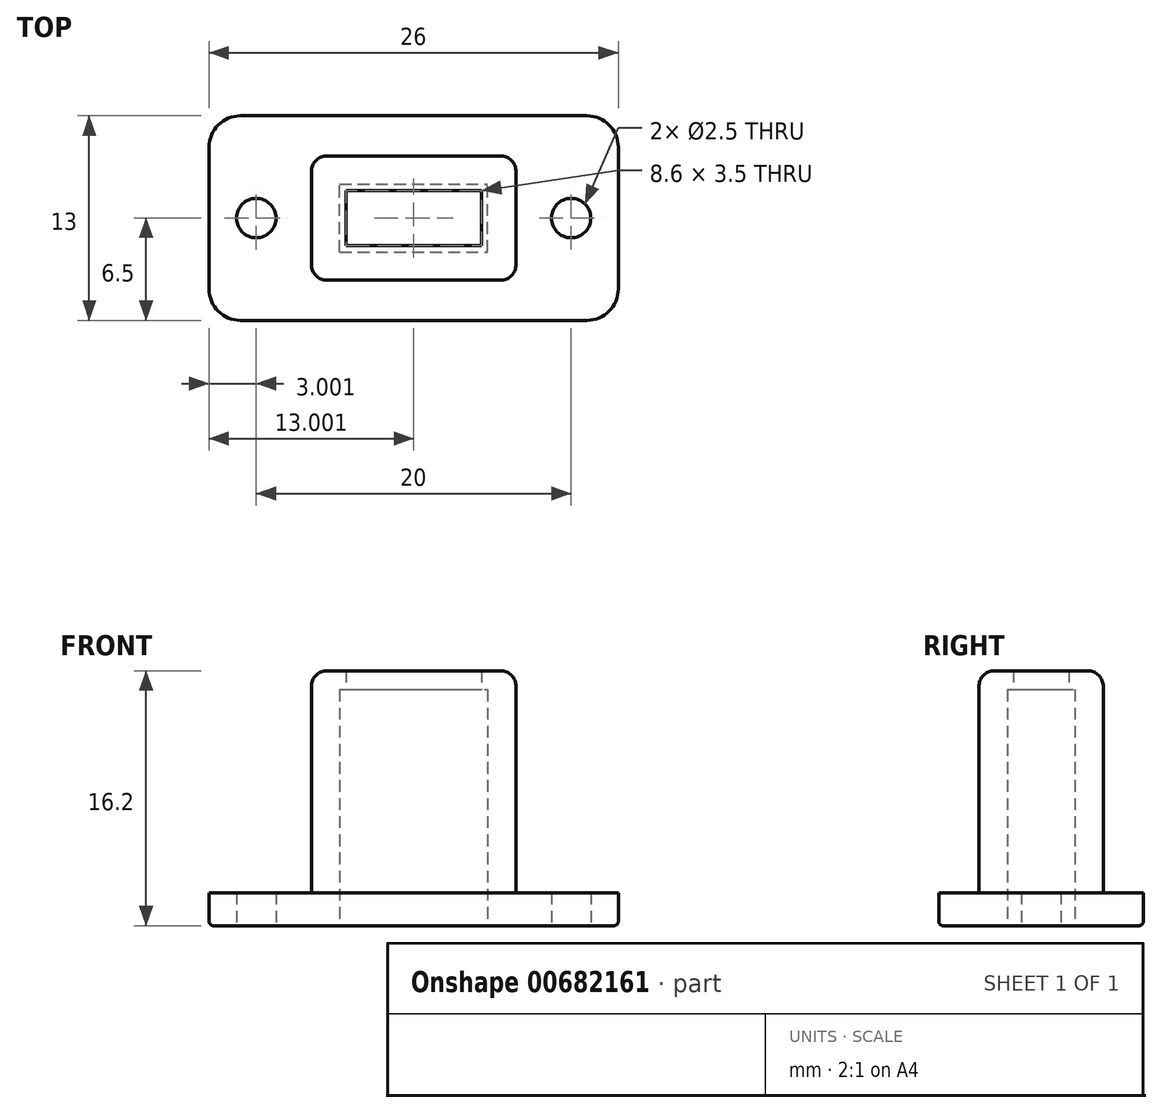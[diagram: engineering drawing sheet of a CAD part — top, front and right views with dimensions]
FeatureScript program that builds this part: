
annotation { "Feature Type Name" : "Feature", "Feature Type Description" : "" }
export const myFeature = defineFeature(function(context is Context, id is Id, definition is map)
    precondition{}
    {
        {
            var Q0;
            Q0=qCreatedBy(makeId("Top.planeOp"),FACE);
            var sketch = newSketch(context, id + "F0", { "sketchPlane" : qUnion([Q0])});
            skLineSegment(sketch, "E0.bottom", {"start": v(-13.44, 13) * mm, "end": v(8.56, 13) * mm});
            skLineSegment(sketch, "E0.top", {"start": v(-13.44, 0) * mm, "end": v(8.56, 0) * mm});
            skLineSegment(sketch, "E0.left", {"start": v(-15.44, 11) * mm, "end": v(-15.44, 2) * mm});
            skLineSegment(sketch, "E0.right", {"start": v(10.56, 11) * mm, "end": v(10.56, 2) * mm});
            skCircle(sketch, "E1", {"center": v(-12.44, 6.5) * mm, "radius": 1.25 * mm});
            skCircle(sketch, "E2", {"center": v(7.56, 6.5) * mm, "radius": 1.25 * mm});
            skPoint(sketch, "E3.visualSharp", {"position": v(-15.44, 13) * mm});
            skArc(sketch, "E3.filletArc", {"start": v(-13.44, 13) * mm, "mid": v(-14.85, 12.41) * mm, "end": v(-15.44, 11) * mm});
            skPoint(sketch, "E4.visualSharp", {"position": v(-15.44, 0) * mm});
            skArc(sketch, "E4.filletArc", {"start": v(-15.44, 2) * mm, "mid": v(-14.85, 0.59) * mm, "end": v(-13.44, 0) * mm});
            skPoint(sketch, "E5.visualSharp", {"position": v(10.56, 13) * mm});
            skArc(sketch, "E5.filletArc", {"start": v(10.56, 11) * mm, "mid": v(9.98, 12.41) * mm, "end": v(8.56, 13) * mm});
            skPoint(sketch, "E6.visualSharp", {"position": v(10.56, 0) * mm});
            skArc(sketch, "E6.filletArc", {"start": v(8.56, 0) * mm, "mid": v(9.98, 0.59) * mm, "end": v(10.56, 2) * mm});
            skSolve(sketch);
        }
        {
            var Q0;
            Q0 = qSketchRegion(id + "F0", true);
            extrude(context, id + "F1", {"entities" : qUnion([Q0]), "depth" : 2.1 * mm, "offsetDistance" : 25 * mm});
        }
        {
            var Q0;
            Q0=makeQuery(id+"F1.opExtrude","CAP_FACE",FACE,{"disambiguationData":[OSD([sQuery(id+"F0.wireOp",EDGE,"E0.bottom"),sQuery(id+"F0.wireOp",EDGE,"E0.top"),sQuery(id+"F0.wireOp",EDGE,"E0.left"),sQuery(id+"F0.wireOp",EDGE,"E0.right"),sQuery(id+"F0.wireOp",EDGE,"E1"),sQuery(id+"F0.wireOp",EDGE,"E2"),sQuery(id+"F0.wireOp",EDGE,"E3.filletArc"),sQuery(id+"F0.wireOp",EDGE,"E4.filletArc"),sQuery(id+"F0.wireOp",EDGE,"E5.filletArc"),sQuery(id+"F0.wireOp",EDGE,"E6.filletArc")])],"isStart":true});
            var sketch = newSketch(context, id + "F2", { "sketchPlane" : qUnion([Q0])});
            skLineSegment(sketch, "E7.bottom", {"start": v(-7.14, -4.35) * mm, "end": v(2.26, -4.35) * mm});
            skLineSegment(sketch, "E7.top", {"start": v(-7.14, -8.65) * mm, "end": v(2.26, -8.65) * mm});
            skLineSegment(sketch, "E7.left", {"start": v(-7.14, -4.35) * mm, "end": v(-7.14, -8.65) * mm});
            skLineSegment(sketch, "E7.right", {"start": v(2.26, -4.35) * mm, "end": v(2.26, -8.65) * mm});
            skLineSegment(sketch, "E8", {"start": v(-7.14, -4.35) * mm, "end": v(-15.44, -4.35) * mm, "construction": true});
            skLineSegment(sketch, "E9", {"start": v(2.26, -4.35) * mm, "end": v(10.56, -4.35) * mm, "construction": true});
            skLineSegment(sketch, "E10", {"start": v(-7.14, -4.35) * mm, "end": v(-7.14, 0) * mm, "construction": true});
            skLineSegment(sketch, "E11", {"start": v(-7.14, -8.65) * mm, "end": v(-7.14, -13) * mm, "construction": true});
            skSolve(sketch);
        }
        {
            var Q0;
            Q0 = qSketchRegion(id + "F2", true);
            extrude(context, id + "F3", {"entities" : qUnion([Q0]), "oppositeDirection" : true, "depth" : 15 * mm, "offsetDistance" : 25 * mm});
        }
        {
            var Q0;
            Q0=makeQuery(id+"F1.opExtrude","CAP_FACE",FACE,{"disambiguationData":[OSD([sQuery(id+"F0.wireOp",EDGE,"E0.bottom"),sQuery(id+"F0.wireOp",EDGE,"E0.top"),sQuery(id+"F0.wireOp",EDGE,"E0.left"),sQuery(id+"F0.wireOp",EDGE,"E0.right"),sQuery(id+"F0.wireOp",EDGE,"E1"),sQuery(id+"F0.wireOp",EDGE,"E2"),sQuery(id+"F0.wireOp",EDGE,"E3.filletArc"),sQuery(id+"F0.wireOp",EDGE,"E4.filletArc"),sQuery(id+"F0.wireOp",EDGE,"E5.filletArc"),sQuery(id+"F0.wireOp",EDGE,"E6.filletArc")])],"isStart":false});
            var sketch = newSketch(context, id + "F4", { "sketchPlane" : qUnion([Q0])});
            skLineSegment(sketch, "E12.0", {"start": v(-7.14, 4.35) * mm, "end": v(2.26, 4.35) * mm, "construction": true});
            skPoint(sketch, "E13.0", {"position": v(2.26, 6.5) * mm});
            skLineSegment(sketch, "E14.0", {"start": v(2.26, 4.35) * mm, "end": v(2.26, 8.65) * mm, "construction": true});
            skLineSegment(sketch, "E15.0", {"start": v(-7.14, 8.65) * mm, "end": v(2.26, 8.65) * mm, "construction": true});
            skLineSegment(sketch, "E16.0", {"start": v(-7.14, 4.35) * mm, "end": v(-7.14, 8.65) * mm, "construction": true});
            skLineSegment(sketch, "E17.0", {"start": v(-8.94, 2.55) * mm, "end": v(-8.94, 10.45) * mm});
            skLineSegment(sketch, "E17.1", {"start": v(-8.94, 2.55) * mm, "end": v(4.06, 2.55) * mm});
            skLineSegment(sketch, "E17.2", {"start": v(4.06, 2.55) * mm, "end": v(4.06, 10.45) * mm});
            skLineSegment(sketch, "E17.3", {"start": v(-8.94, 10.45) * mm, "end": v(4.06, 10.45) * mm});
            skSolve(sketch);
        }
        {
            var Q0;
            Q0=makeQuery(id+"F4.imprint","IMPRINT",FACE,{"disambiguationData":[TD([[makeQuery(id+"F4.imprint","IMPRINT",EDGE,{"derivedFrom":sQuery(id+"F4.wireOp",EDGE,"E17.0")}),-1.0]])]});
            var Q1;
            Q1=makeQuery(id+"F3.opExtrude","CAP_FACE",FACE,{"disambiguationData":[OSD([sQuery(id+"F2.wireOp",EDGE,"E7.bottom"),sQuery(id+"F2.wireOp",EDGE,"E7.top"),sQuery(id+"F2.wireOp",EDGE,"E7.left"),sQuery(id+"F2.wireOp",EDGE,"E7.right")])],"isStart":false});
            extrude(context, id + "F5", {"entities" : qUnion([Q0]), "endBound" : BoundingType.UP_TO_SURFACE, "depth" : 25 * mm, "endBoundEntityFace" : qUnion([Q1]), "offsetDistance" : 25 * mm});
        }
        {
            var Q0;
            Q0=makeQuery(id+"F5.opExtrude","CAP_FACE",FACE,{"disambiguationData":[OSD([sQuery(id+"F4.wireOp",EDGE,"E17.0"),sQuery(id+"F4.wireOp",EDGE,"E17.1"),sQuery(id+"F4.wireOp",EDGE,"E17.2"),sQuery(id+"F4.wireOp",EDGE,"E17.3")])],"isStart":false});
            var sketch = newSketch(context, id + "F6", { "sketchPlane" : qUnion([Q0])});
            skLineSegment(sketch, "E18.0", {"start": v(4.06, 2.55) * mm, "end": v(-8.94, 2.55) * mm});
            skLineSegment(sketch, "E19.0", {"start": v(-8.94, 10.45) * mm, "end": v(-8.94, 2.55) * mm});
            skLineSegment(sketch, "E20.0", {"start": v(4.06, 10.45) * mm, "end": v(-8.94, 10.45) * mm});
            skLineSegment(sketch, "E21.0", {"start": v(4.06, 10.45) * mm, "end": v(4.06, 2.55) * mm});
            skSolve(sketch);
        }
        {
            var Q0;
            Q0 = qSketchRegion(id + "F6", true);
            extrude(context, id + "F7", {"entities" : qUnion([Q0]), "depth" : 1.2 * mm, "offsetDistance" : 25 * mm});
        }
        {
            var Q0;
            Q0=makeQuery(id+"F5.opExtrude","CAP_FACE",FACE,{"disambiguationData":[OSD([sQuery(id+"F4.wireOp",EDGE,"E17.0"),sQuery(id+"F4.wireOp",EDGE,"E17.1"),sQuery(id+"F4.wireOp",EDGE,"E17.2"),sQuery(id+"F4.wireOp",EDGE,"E17.3")])],"isStart":false});
            var sketch = newSketch(context, id + "F8", { "sketchPlane" : qUnion([Q0])});
            skLineSegment(sketch, "E22.0", {"start": v(-7.14, 4.35) * mm, "end": v(2.26, 4.35) * mm, "construction": true});
            skLineSegment(sketch, "E23.0", {"start": v(2.26, 4.35) * mm, "end": v(2.26, 8.65) * mm, "construction": true});
            skLineSegment(sketch, "E24.0", {"start": v(-7.14, 8.65) * mm, "end": v(2.26, 8.65) * mm, "construction": true});
            skPoint(sketch, "E25.0", {"position": v(-7.14, 6.5) * mm});
            skLineSegment(sketch, "E26", {"start": v(-7.14, 4.35) * mm, "end": v(-7.14, 8.65) * mm, "construction": true});
            skLineSegment(sketch, "E27.0", {"start": v(-6.74, 4.75) * mm, "end": v(1.86, 4.75) * mm});
            skLineSegment(sketch, "E27.1", {"start": v(-6.74, 4.75) * mm, "end": v(-6.74, 8.25) * mm});
            skLineSegment(sketch, "E27.2", {"start": v(-6.74, 8.25) * mm, "end": v(1.86, 8.25) * mm});
            skLineSegment(sketch, "E27.3", {"start": v(1.86, 4.75) * mm, "end": v(1.86, 8.25) * mm});
            skSolve(sketch);
        }
        {
            var Q0;
            Q0=makeQuery(id+"F8.imprint","IMPRINT",FACE,{"disambiguationData":[TD([[makeQuery(id+"F8.imprint","IMPRINT",EDGE,{"derivedFrom":sQuery(id+"F8.wireOp",EDGE,"E27.0")}),1.0]])]});
            var Q1;
            Q1=sQuery(id+"F8.wireOp",EDGE,"E27.0");
            var Q2;
            Q2=sQuery(id+"F8.wireOp",EDGE,"E27.3");
            var Q3;
            Q3=sQuery(id+"F8.wireOp",EDGE,"E27.2");
            var Q4;
            Q4=sQuery(id+"F8.wireOp",EDGE,"E27.1");
            extrude(context, id + "F9", {"entities" : qUnion([Q0]), "surfaceEntities" : qUnion([Q1, Q2, Q3, Q4]), "depth" : 25 * mm, "offsetDistance" : 25 * mm});
        }
        {
            var Q0;
            Q0=makeQuery(id+"F9.opExtrude","SWEPT_BODY",BODY,{"disambiguationData":[OSD([sQuery(id+"F8.wireOp",EDGE,"E27.0"),sQuery(id+"F8.wireOp",EDGE,"E27.1"),sQuery(id+"F8.wireOp",EDGE,"E27.2"),sQuery(id+"F8.wireOp",EDGE,"E27.3")])]});
            var Q1;
            Q1=makeQuery(id+"F7.opExtrude","SWEPT_BODY",BODY,{"disambiguationData":[OSD([sQuery(id+"F6.wireOp",EDGE,"E18.0"),sQuery(id+"F6.wireOp",EDGE,"E19.0"),sQuery(id+"F6.wireOp",EDGE,"E20.0"),sQuery(id+"F6.wireOp",EDGE,"E21.0")])]});
            booleanBodies(context, id + "F10", {"operationType" : BooleanOperationType.SUBTRACTION, "tools" : qUnion([Q0]), "targets" : qUnion([Q1])});
        }
        {
            var Q0;
            Q0=makeQuery(id+"F3.opExtrude","SWEPT_BODY",BODY,{"disambiguationData":[OSD([sQuery(id+"F2.wireOp",EDGE,"E7.bottom"),sQuery(id+"F2.wireOp",EDGE,"E7.top"),sQuery(id+"F2.wireOp",EDGE,"E7.left"),sQuery(id+"F2.wireOp",EDGE,"E7.right")])]});
            var Q1;
            Q1=makeQuery(id+"F5.opExtrude","SWEPT_BODY",BODY,{"disambiguationData":[OSD([sQuery(id+"F4.wireOp",EDGE,"E17.0"),sQuery(id+"F4.wireOp",EDGE,"E17.1"),sQuery(id+"F4.wireOp",EDGE,"E17.2"),sQuery(id+"F4.wireOp",EDGE,"E17.3")])]});
            var Q2;
            Q2=makeQuery(id+"F1.opExtrude","SWEPT_BODY",BODY,{"disambiguationData":[OSD([sQuery(id+"F0.wireOp",EDGE,"E0.bottom"),sQuery(id+"F0.wireOp",EDGE,"E0.top"),sQuery(id+"F0.wireOp",EDGE,"E0.left"),sQuery(id+"F0.wireOp",EDGE,"E0.right"),sQuery(id+"F0.wireOp",EDGE,"E1"),sQuery(id+"F0.wireOp",EDGE,"E2"),sQuery(id+"F0.wireOp",EDGE,"E3.filletArc"),sQuery(id+"F0.wireOp",EDGE,"E4.filletArc"),sQuery(id+"F0.wireOp",EDGE,"E5.filletArc"),sQuery(id+"F0.wireOp",EDGE,"E6.filletArc")])]});
            booleanBodies(context, id + "F11", {"operationType" : BooleanOperationType.SUBTRACTION, "tools" : qUnion([Q0]), "targets" : qUnion([Q1, Q2])});
        }
        {
            var Q0;
            Q0=makeQuery(id+"F7.opExtrude","SWEPT_BODY",BODY,{"disambiguationData":[OSD([sQuery(id+"F6.wireOp",EDGE,"E18.0"),sQuery(id+"F6.wireOp",EDGE,"E19.0"),sQuery(id+"F6.wireOp",EDGE,"E20.0"),sQuery(id+"F6.wireOp",EDGE,"E21.0")])]});
            var Q1;
            Q1=makeQuery(id+"F5.opExtrude","SWEPT_BODY",BODY,{"disambiguationData":[OSD([sQuery(id+"F4.wireOp",EDGE,"E17.0"),sQuery(id+"F4.wireOp",EDGE,"E17.1"),sQuery(id+"F4.wireOp",EDGE,"E17.2"),sQuery(id+"F4.wireOp",EDGE,"E17.3")])]});
            var Q2;
            Q2=makeQuery(id+"F1.opExtrude","SWEPT_BODY",BODY,{"disambiguationData":[OSD([sQuery(id+"F0.wireOp",EDGE,"E0.bottom"),sQuery(id+"F0.wireOp",EDGE,"E0.top"),sQuery(id+"F0.wireOp",EDGE,"E0.left"),sQuery(id+"F0.wireOp",EDGE,"E0.right"),sQuery(id+"F0.wireOp",EDGE,"E1"),sQuery(id+"F0.wireOp",EDGE,"E2"),sQuery(id+"F0.wireOp",EDGE,"E3.filletArc"),sQuery(id+"F0.wireOp",EDGE,"E4.filletArc"),sQuery(id+"F0.wireOp",EDGE,"E5.filletArc"),sQuery(id+"F0.wireOp",EDGE,"E6.filletArc")])]});
            booleanBodies(context, id + "F12", {"operationType" : BooleanOperationType.UNION, "tools" : qUnion([Q0, Q1, Q2])});
        }
        {
            var Q0;
            Q0=makeQuery(id+"F5.opExtrude","CAP_EDGE",EDGE,{"disambiguationData":[OSD([sQuery(id+"F4.wireOp",EDGE,"E17.3")])],"isStart":true});
            var Q1;
            Q1=makeQuery(id+"F5.opExtrude","CAP_EDGE",EDGE,{"disambiguationData":[OSD([sQuery(id+"F4.wireOp",EDGE,"E17.2")])],"isStart":true});
            var Q2;
            Q2=makeQuery(id+"F5.opExtrude","CAP_EDGE",EDGE,{"disambiguationData":[OSD([sQuery(id+"F4.wireOp",EDGE,"E17.0")])],"isStart":true});
            var Q3;
            Q3=makeQuery(id+"F5.opExtrude","CAP_EDGE",EDGE,{"disambiguationData":[OSD([sQuery(id+"F4.wireOp",EDGE,"E17.1")])],"isStart":true});
            var Q4;
            Q4=makeQuery(id+"F12.opBoolean","MERGE",EDGE,{"derivedFrom":[makeQuery(id+"F5.opExtrude","SWEPT_EDGE",EDGE,{"disambiguationData":[OSD([sQuery(id+"F4.wireOp",EDGE,"E17.0"),sQuery(id+"F4.wireOp",EDGE,"E17.3")])]}),makeQuery(id+"F7.opExtrude","SWEPT_EDGE",EDGE,{"disambiguationData":[OSD([sQuery(id+"F6.wireOp",EDGE,"E19.0"),sQuery(id+"F6.wireOp",EDGE,"E20.0")])]})]});
            var Q5;
            Q5=makeQuery(id+"F12.opBoolean","MERGE",EDGE,{"derivedFrom":[makeQuery(id+"F5.opExtrude","SWEPT_EDGE",EDGE,{"disambiguationData":[OSD([sQuery(id+"F4.wireOp",EDGE,"E17.0"),sQuery(id+"F4.wireOp",EDGE,"E17.1")])]}),makeQuery(id+"F7.opExtrude","SWEPT_EDGE",EDGE,{"disambiguationData":[OSD([sQuery(id+"F6.wireOp",EDGE,"E18.0"),sQuery(id+"F6.wireOp",EDGE,"E19.0")])]})]});
            var Q6;
            Q6=makeQuery(id+"F12.opBoolean","MERGE",EDGE,{"derivedFrom":[makeQuery(id+"F5.opExtrude","SWEPT_EDGE",EDGE,{"disambiguationData":[OSD([sQuery(id+"F4.wireOp",EDGE,"E17.2"),sQuery(id+"F4.wireOp",EDGE,"E17.3")])]}),makeQuery(id+"F7.opExtrude","SWEPT_EDGE",EDGE,{"disambiguationData":[OSD([sQuery(id+"F6.wireOp",EDGE,"E20.0"),sQuery(id+"F6.wireOp",EDGE,"E21.0")])]})]});
            var Q7;
            Q7=makeQuery(id+"F12.opBoolean","MERGE",EDGE,{"derivedFrom":[makeQuery(id+"F5.opExtrude","SWEPT_EDGE",EDGE,{"disambiguationData":[OSD([sQuery(id+"F4.wireOp",EDGE,"E17.1"),sQuery(id+"F4.wireOp",EDGE,"E17.2")])]}),makeQuery(id+"F7.opExtrude","SWEPT_EDGE",EDGE,{"disambiguationData":[OSD([sQuery(id+"F6.wireOp",EDGE,"E18.0"),sQuery(id+"F6.wireOp",EDGE,"E21.0")])]})]});
            var Q8;
            Q8=makeQuery(id+"F7.opExtrude","CAP_EDGE",EDGE,{"disambiguationData":[OSD([sQuery(id+"F6.wireOp",EDGE,"E19.0")])],"isStart":false});
            var Q9;
            Q9=makeQuery(id+"F7.opExtrude","CAP_EDGE",EDGE,{"disambiguationData":[OSD([sQuery(id+"F6.wireOp",EDGE,"E20.0")])],"isStart":false});
            var Q10;
            Q10=makeQuery(id+"F7.opExtrude","CAP_EDGE",EDGE,{"disambiguationData":[OSD([sQuery(id+"F6.wireOp",EDGE,"E18.0")])],"isStart":false});
            var Q11;
            Q11=makeQuery(id+"F7.opExtrude","CAP_EDGE",EDGE,{"disambiguationData":[OSD([sQuery(id+"F6.wireOp",EDGE,"E21.0")])],"isStart":false});
            fillet(context, id + "F13", {"entities" : qUnion([Q0, Q1, Q2, Q3, Q4, Q5, Q6, Q7, Q8, Q9, Q10, Q11]), "radius" : 1 * mm, "tangentPropagation" : true, "allowEdgeOverflow" : false});
        }
        {
            var Q0;
            Q0=makeQuery(id+"F11.opBoolean","COPY",EDGE,{"derivedFrom":makeQuery(id+"F3.opExtrude","CAP_EDGE",EDGE,{"disambiguationData":[OSD([sQuery(id+"F2.wireOp",EDGE,"E7.right")])],"isStart":true})});
            var Q1;
            Q1=makeQuery(id+"F11.opBoolean","COPY",EDGE,{"derivedFrom":makeQuery(id+"F3.opExtrude","CAP_EDGE",EDGE,{"disambiguationData":[OSD([sQuery(id+"F2.wireOp",EDGE,"E7.top")])],"isStart":true})});
            var Q2;
            Q2=makeQuery(id+"F11.opBoolean","COPY",EDGE,{"derivedFrom":makeQuery(id+"F3.opExtrude","CAP_EDGE",EDGE,{"disambiguationData":[OSD([sQuery(id+"F2.wireOp",EDGE,"E7.left")])],"isStart":true})});
            var Q3;
            Q3=makeQuery(id+"F11.opBoolean","COPY",EDGE,{"derivedFrom":makeQuery(id+"F3.opExtrude","CAP_EDGE",EDGE,{"disambiguationData":[OSD([sQuery(id+"F2.wireOp",EDGE,"E7.bottom")])],"isStart":true})});
            var Q4;
            Q4=makeQuery(id+"F1.opExtrude","CAP_EDGE",EDGE,{"disambiguationData":[OSD([sQuery(id+"F0.wireOp",EDGE,"E0.bottom")])],"isStart":true});
            fillet(context, id + "F14", {"entities" : qUnion([Q0, Q1, Q2, Q3, Q4]), "radius" : 0.3 * mm, "tangentPropagation" : true, "allowEdgeOverflow" : false});
        }
    });
